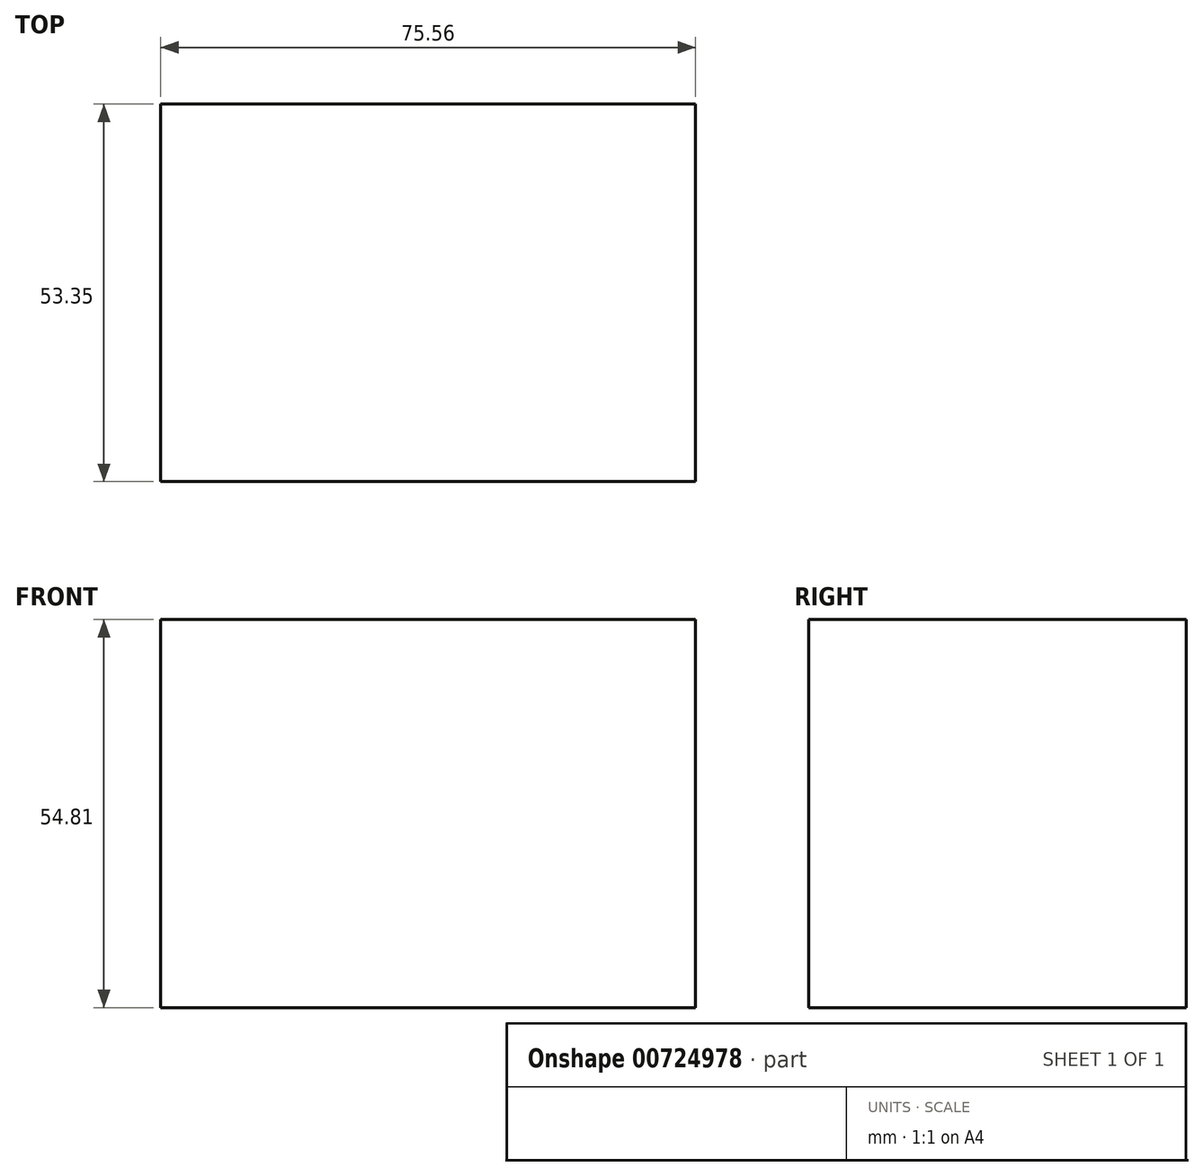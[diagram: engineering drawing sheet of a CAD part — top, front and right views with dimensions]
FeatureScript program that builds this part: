
annotation { "Feature Type Name" : "Feature", "Feature Type Description" : "" }
export const myFeature = defineFeature(function(context is Context, id is Id, definition is map)
    precondition{}
    {
        {
            var Q0;
            Q0=qCreatedBy(makeId("Right.planeOp"),FACE);
            var sketch = newSketch(context, id + "F0", { "sketchPlane" : qUnion([Q0])});
            skLineSegment(sketch, "E0.bottom", {"start": v(53.35, 54.81) * mm, "end": v(0, 54.81) * mm});
            skLineSegment(sketch, "E0.top", {"start": v(53.35, 0) * mm, "end": v(0, 0) * mm});
            skLineSegment(sketch, "E0.left", {"start": v(53.35, 54.81) * mm, "end": v(53.35, 0) * mm});
            skLineSegment(sketch, "E0.right", {"start": v(0, 54.81) * mm, "end": v(0, 0) * mm});
            skSolve(sketch);
        }
        {
            var Q0;
            Q0=makeQuery(id+"F0.imprint","IMPRINT",FACE,{"disambiguationData":[TD([[makeQuery(id+"F0.imprint","IMPRINT",EDGE,{"derivedFrom":sQuery(id+"F0.wireOp",EDGE,"E0.bottom")}),1.0]])]});
            extrude(context, id + "F1", {"entities" : qUnion([Q0]), "depth" : 75.56 * mm, "offsetDistance" : 25.4 * mm});
        }
    });
